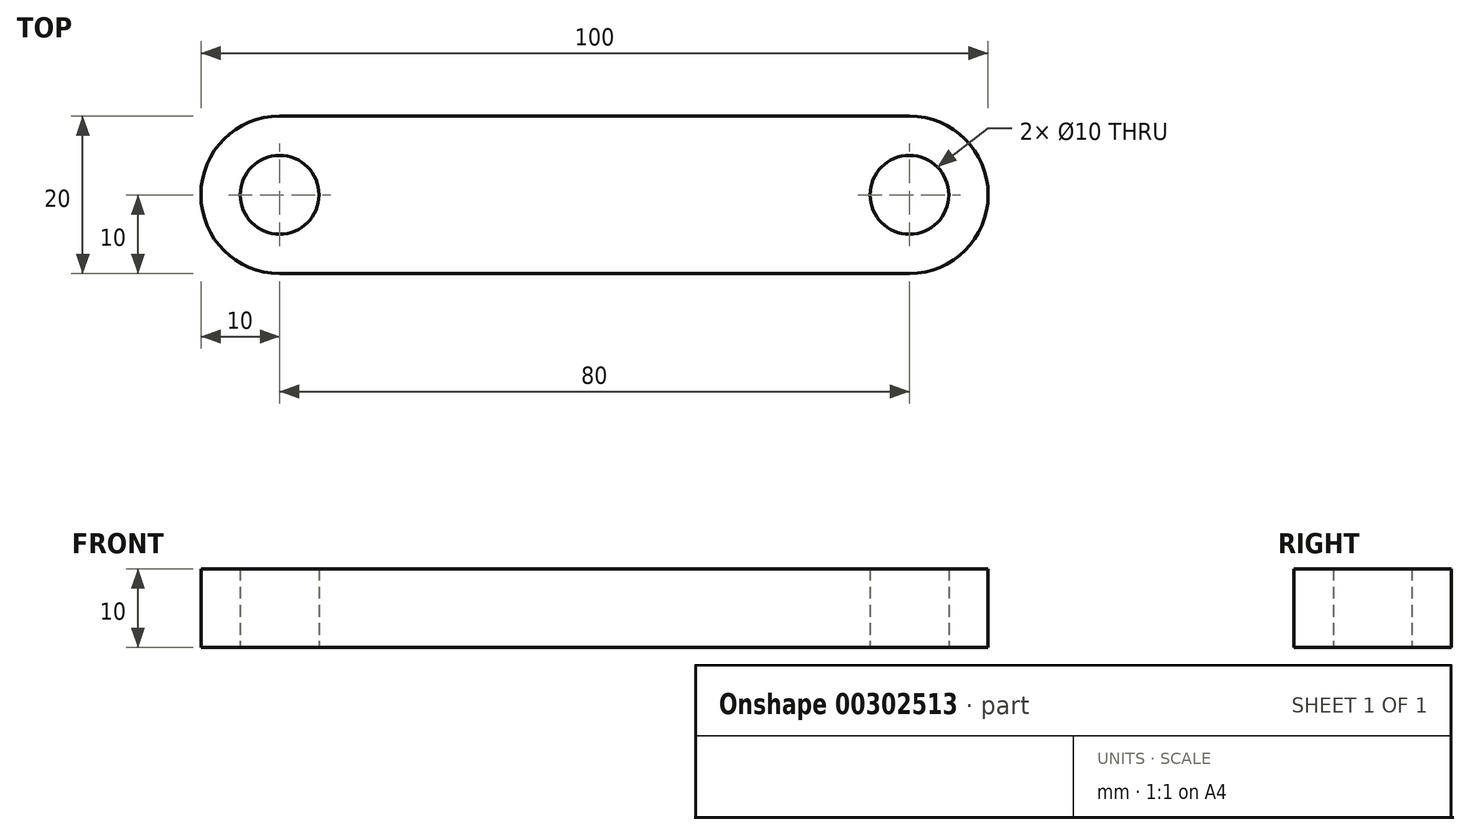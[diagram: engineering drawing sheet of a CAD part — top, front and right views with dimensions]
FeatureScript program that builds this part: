
annotation { "Feature Type Name" : "Feature", "Feature Type Description" : "" }
export const myFeature = defineFeature(function(context is Context, id is Id, definition is map)
    precondition{}
    {
        {
            var Q0;
            Q0=qCreatedBy(makeId("Top.planeOp"),FACE);
            var sketch = newSketch(context, id + "F0", { "sketchPlane" : qUnion([Q0])});
            skLineSegment(sketch, "E0", {"start": v(0, 0) * mm, "end": v(80, 0) * mm});
            skLineSegment(sketch, "E1", {"start": v(0, 20) * mm, "end": v(80, 20) * mm});
            skArc(sketch, "E2", {"start": v(0, 20) * mm, "mid": v(-10, 10) * mm, "end": v(0, 0) * mm});
            skArc(sketch, "E3", {"start": v(80, 0) * mm, "mid": v(90, 10) * mm, "end": v(80, 20) * mm});
            skCircle(sketch, "E4", {"center": v(80, 10) * mm, "radius": 5 * mm});
            skCircle(sketch, "E5", {"center": v(0, 10) * mm, "radius": 5 * mm});
            skSolve(sketch);
        }
        {
            var Q0;
            Q0=makeQuery(id+"F0.imprint","IMPRINT",FACE,{"disambiguationData":[TD([[makeQuery(id+"F0.imprint","IMPRINT",EDGE,{"derivedFrom":sQuery(id+"F0.wireOp",EDGE,"E0")}),1.0]])]});
            extrude(context, id + "F1", {"entities" : qUnion([Q0]), "depth" : 10 * mm, "symmetric" : true});
        }
    });
